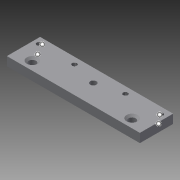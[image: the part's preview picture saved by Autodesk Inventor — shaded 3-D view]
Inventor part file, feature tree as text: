
AUTODESK INVENTOR PART (.ipt)
format: ipt  version: 2015 SP1 (Build 190203100, 203)  size: 342,016 bytes
history: native  units: mm
features: hole x6, pattern_linear x2, extrude x1, sketch x1
ambient origin geometry x8: Origin, YZ Plane, XZ Plane, XY Plane, X Axis, Y Axis, Z Axis, Center Point
bodies: Solid1 (feature_tree)
feature tree (10):
  extrude  "Extrusion1"  Depth=8.0mm TaperAngle=0.0deg
  hole  "Hole1"  [1 undecoded]
  hole  "Hole2"  [1 undecoded]
  hole  "Hole3"  [1 undecoded]
  hole  "Hole4"  [1 undecoded]
  hole  "Hole5"  [1 undecoded]
  hole  "Hole6"  [1 undecoded]
  pattern_linear  "Rectangular Pattern1"  Spacing1=0.0mm  [1 undecoded]
  pattern_linear  "Rectangular Pattern2"  Spacing1=6.0mm  [1 undecoded]
  sketch  "Sketch1"  dims[d1=30.0mm d2=8.0mm d3=0.0mm d4=15.0mm d5=8.0mm d6=6.5mm d7=6.0mm d8=10.0mm d9=2.0mm d10=90.0deg d11=8.0mm d12=20.594885mm d13=15.0mm d14=8.0mm d15=6.5mm d16=6.0mm d17=10.0mm d18=2.0mm d19=90.0deg d20=8.0mm d21=20.594885mm d22=60.0mm d23=12.0mm d24=16.0mm d25=10.0mm d26=10.0mm d27=2.0mm d28=90.0deg d29=5.0mm d30=0.0mm d31=10.0mm d32=10.0mm d33=5.5mm d34=16.0mm d35=10.0mm d36=2.0mm d37=90.0deg d38=22.2mm d39=20.594885mm d40=5.0mm d41=6.0mm d42=4.134mm d43=10.0mm d44=10.0mm d45=2.0mm d46=90.0deg d47=14.2mm d48=20.594885mm d49=0.0mm d50=0.0mm d51=6.0mm d52=5.0mm d53=4.134mm d54=10.0mm d55=10.0mm d56=2.0mm d57=90.0deg d58=14.2mm d59=20.594885mm d60=0.0mm d61=0.0mm d62=20.0mm d64=32.0mm d65=20.0mm d67=32.0mm]
note: 8 required parameter values undecoded (feature->parameter linkage not recoverable at this tier; creation-order binding heuristic only, values carry confidence <= 0.55)
